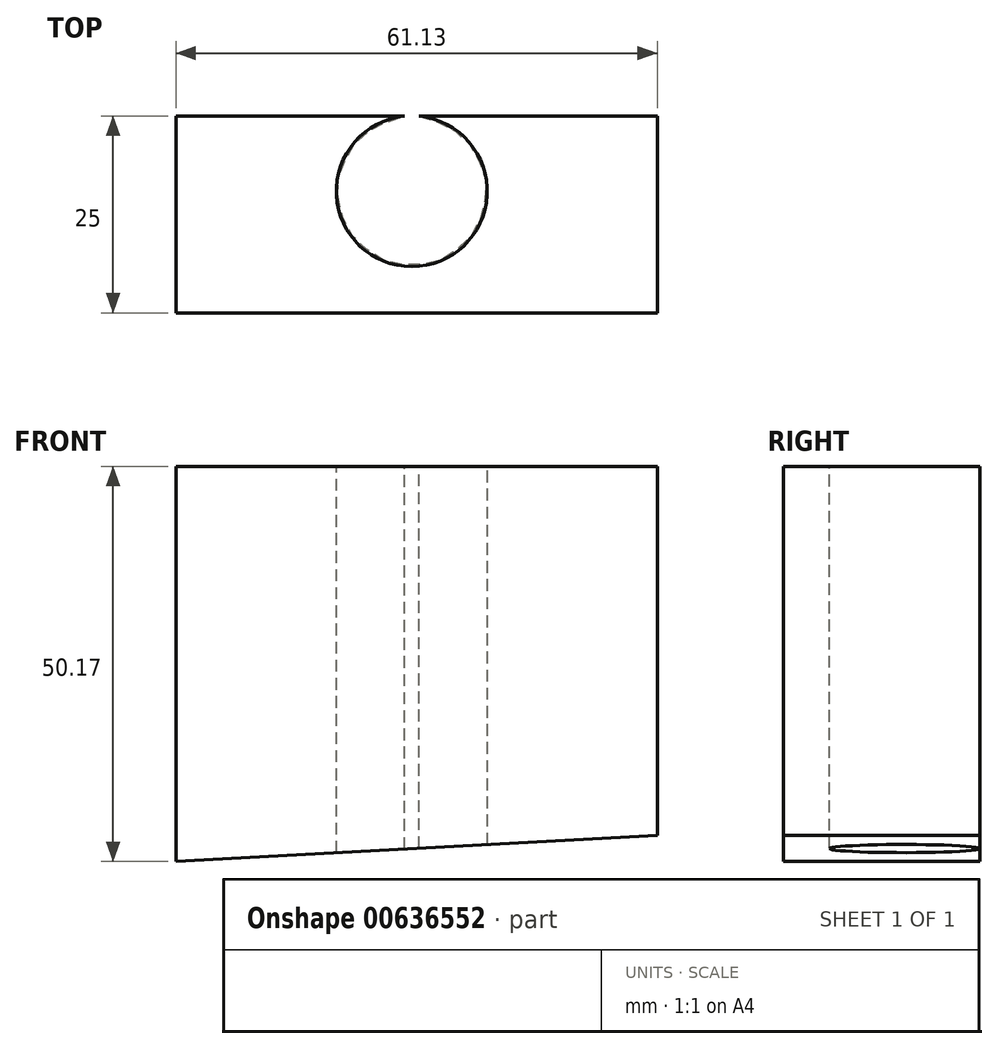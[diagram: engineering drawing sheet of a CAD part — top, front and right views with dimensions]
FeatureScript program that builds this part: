
annotation { "Feature Type Name" : "Feature", "Feature Type Description" : "" }
export const myFeature = defineFeature(function(context is Context, id is Id, definition is map)
    precondition{}
    {
        {
            var Q0;
            Q0=qCreatedBy(makeId("Front.planeOp"),FACE);
            var sketch = newSketch(context, id + "F0", { "sketchPlane" : qUnion([Q0])});
            skLineSegment(sketch, "E0", {"start": v(0, 0) * mm, "end": v(0, 50.17) * mm});
            skLineSegment(sketch, "E1", {"start": v(0, 50.17) * mm, "end": v(61.13, 50.17) * mm});
            skLineSegment(sketch, "E2", {"start": v(61.13, 50.17) * mm, "end": v(61.13, 3.31) * mm});
            skLineSegment(sketch, "E3", {"start": v(61.13, 3.31) * mm, "end": v(0, 0) * mm});
            skSolve(sketch);
        }
        {
            var Q0;
            Q0 = qSketchRegion(id + "F0", true);
            extrude(context, id + "F1", {"entities" : qUnion([Q0]), "depth" : 25 * mm, "offsetDistance" : 25 * mm});
        }
        {
            var Q0;
            Q0=makeQuery(id+"F1.opExtrude","SWEPT_FACE",FACE,{"disambiguationData":[OSD([sQuery(id+"F0.wireOp",EDGE,"E1")])]});
            var sketch = newSketch(context, id + "F2", { "sketchPlane" : qUnion([Q0])});
            skCircle(sketch, "E4", {"center": v(29.94, -9.54) * mm, "radius": 9.58 * mm});
            skSolve(sketch);
        }
        {
            var Q0;
            Q0 = qSketchRegion(id + "F2", true);
            extrude(context, id + "F3", {"entities" : qUnion([Q0]), "operationType" : NewBodyOperationType.REMOVE, "oppositeDirection" : true, "depth" : 60 * mm, "offsetDistance" : 25 * mm});
        }
    });
